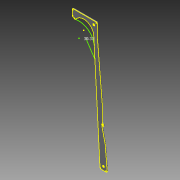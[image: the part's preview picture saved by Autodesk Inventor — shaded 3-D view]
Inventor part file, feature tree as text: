
AUTODESK INVENTOR PART (.ipt)
format: ipt  version: 2013 (Build 170138000, 138)  size: 140,288 bytes
history: native  units: in
note: dims shown in document units (in); Inventor stores cm internally (conversion verified against a paired STEP export)
features: sketch x2, extrude x1, fillet x1
ambient origin geometry x8: Origin, YZ Plane, XZ Plane, XY Plane, X Axis, Y Axis, Z Axis, Center Point
feature tree (4):
  extrude  "Extrusion4"  Depth=2.0in
  fillet  "Fillet1"  Radius=2.0in
  sketch  "Sketch2"  dims[d27=0.125in d28=0.0in d29=0.125in d30=0.2084in]
  sketch  "Sketch1"  dims[d0=2.75in d1=30.0deg d2=2.25in d3=1.0in d4=15.5in d5=0.25in d6=0.5in d7=0.5in d8=0.1875in d9=0.3in d10=5.425in d11=0.25in d12=0.5in d13=0.5in d23=2.0in d24=2.0in]
